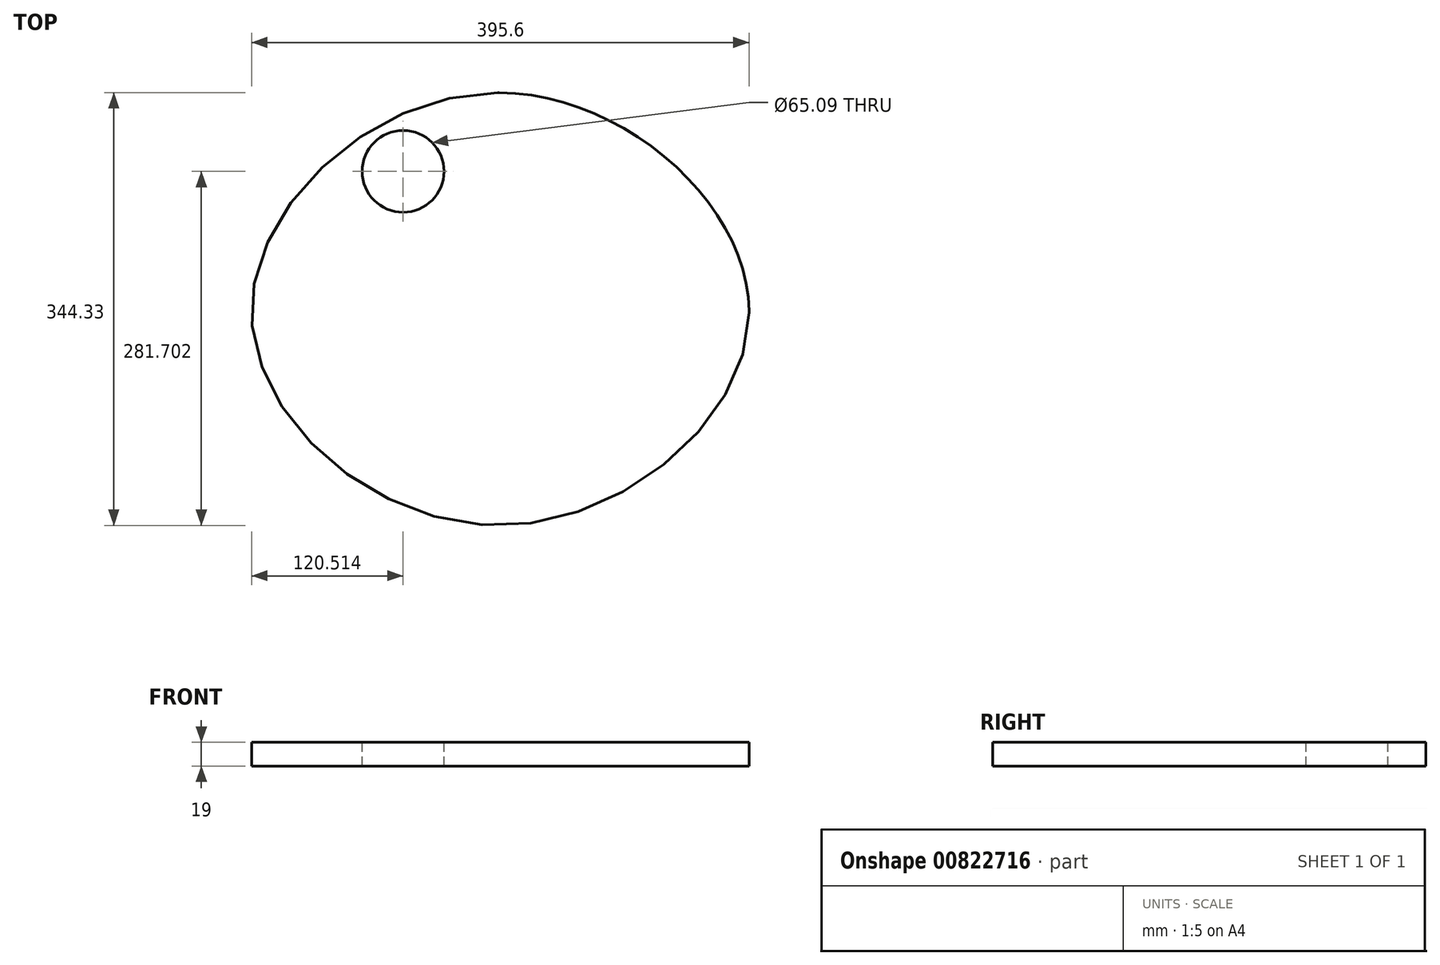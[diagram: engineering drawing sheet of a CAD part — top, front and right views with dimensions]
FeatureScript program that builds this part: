
annotation { "Feature Type Name" : "Feature", "Feature Type Description" : "" }
export const myFeature = defineFeature(function(context is Context, id is Id, definition is map)
    precondition{}
    {
        {
            var Q0;
            Q0=qCreatedBy(makeId("Top.planeOp"),FACE);
            var sketch = newSketch(context, id + "F0", { "sketchPlane" : qUnion([Q0])});
            skLineSegment(sketch, "E0.bottom", {"start": v(200, -175) * mm, "end": v(-200, -175) * mm});
            skLineSegment(sketch, "E0.top", {"start": v(200, 175) * mm, "end": v(-200, 175) * mm});
            skLineSegment(sketch, "E0.left", {"start": v(200, -175) * mm, "end": v(200, 175) * mm});
            skLineSegment(sketch, "E0.right", {"start": v(-200, -175) * mm, "end": v(-200, 175) * mm});
            skPoint(sketch, "E0.middle", {"position": v(0, 0) * mm});
            skSolve(sketch);
        }
        {
            var Q0;
            Q0 = qSketchRegion(id + "F0", true);
            extrude(context, id + "F1", {"entities" : qUnion([Q0]), "depth" : 19 * mm, "offsetDistance" : 25 * mm});
        }
        {
            var Q0;
            Q0=makeQuery(id+"F1.opExtrude","CAP_FACE",FACE,{"disambiguationData":[OSD([sQuery(id+"F0.wireOp",EDGE,"E0.bottom"),sQuery(id+"F0.wireOp",EDGE,"E0.top"),sQuery(id+"F0.wireOp",EDGE,"E0.left"),sQuery(id+"F0.wireOp",EDGE,"E0.right")])],"isStart":false});
            var sketch = newSketch(context, id + "F2", { "sketchPlane" : qUnion([Q0])});
            skPoint(sketch, "E1.1.internal.snap0", {"position": v(-200, 0) * mm});
            skPoint(sketch, "E1.2.internal.snap0", {"position": v(0, -175) * mm});
            skFitSpline(sketch, "E1", {"points": [v(0, 175) * mm, v(-195.6, 0) * mm, v(0, -169.33) * mm, v(200, 0) * mm, v(0, 175) * mm]});
            skCircle(sketch, "E2", {"center": v(-75.09, 112.37) * mm, "radius": 32.54 * mm});
            skSolve(sketch);
        }
        {
            var Q0;
            {var subQ0=sQuery(id+"F2.wireOp",EDGE,"E1");var subQ1=makeQuery(id+"F1.opExtrude","CAP_EDGE",EDGE,{"disambiguationData":[OSD([sQuery(id+"F0.wireOp",EDGE,"E0.left")])],"isStart":false});var subQ2=makeQuery(id+"F2.imprint","INTERSECT",VERTEX,{"disambiguationData":[OD(1.0)],"derivedFrom":[subQ1,subQ0]});Q0=makeQuery(id+"F2.imprint","IMPRINT",FACE,{"disambiguationData":[TD([[makeQuery(id+"F2.imprint","IMPRINT",EDGE,{"disambiguationData":[TD([[subQ2,-1.0]])],"derivedFrom":subQ0}),-1.0]])]});}
            var Q1;
            {var subQ4=makeQuery(id+"F1.opExtrude","CAP_EDGE",EDGE,{"disambiguationData":[OSD([sQuery(id+"F0.wireOp",EDGE,"E0.bottom")])],"isStart":false});Q1=makeQuery(id+"F2.imprint","IMPRINT",FACE,{"disambiguationData":[TD([[makeQuery(id+"F2.imprint","IMPRINT",EDGE,{"derivedFrom":subQ4}),-1.0]])]});}
            extrude(context, id + "F3", {"entities" : qUnion([Q0, Q1]), "operationType" : NewBodyOperationType.REMOVE, "oppositeDirection" : true, "depth" : 25 * mm, "offsetDistance" : 25 * mm});
        }
        {
            var Q0;
            Q0=makeQuery(id+"F2.imprint","IMPRINT",FACE,{"disambiguationData":[TD([[makeQuery(id+"F2.imprint","IMPRINT",EDGE,{"derivedFrom":sQuery(id+"F2.wireOp",EDGE,"E2")}),1.0]])]});
            extrude(context, id + "F4", {"entities" : qUnion([Q0]), "operationType" : NewBodyOperationType.REMOVE, "oppositeDirection" : true, "depth" : 25 * mm, "offsetDistance" : 25 * mm});
        }
    });
